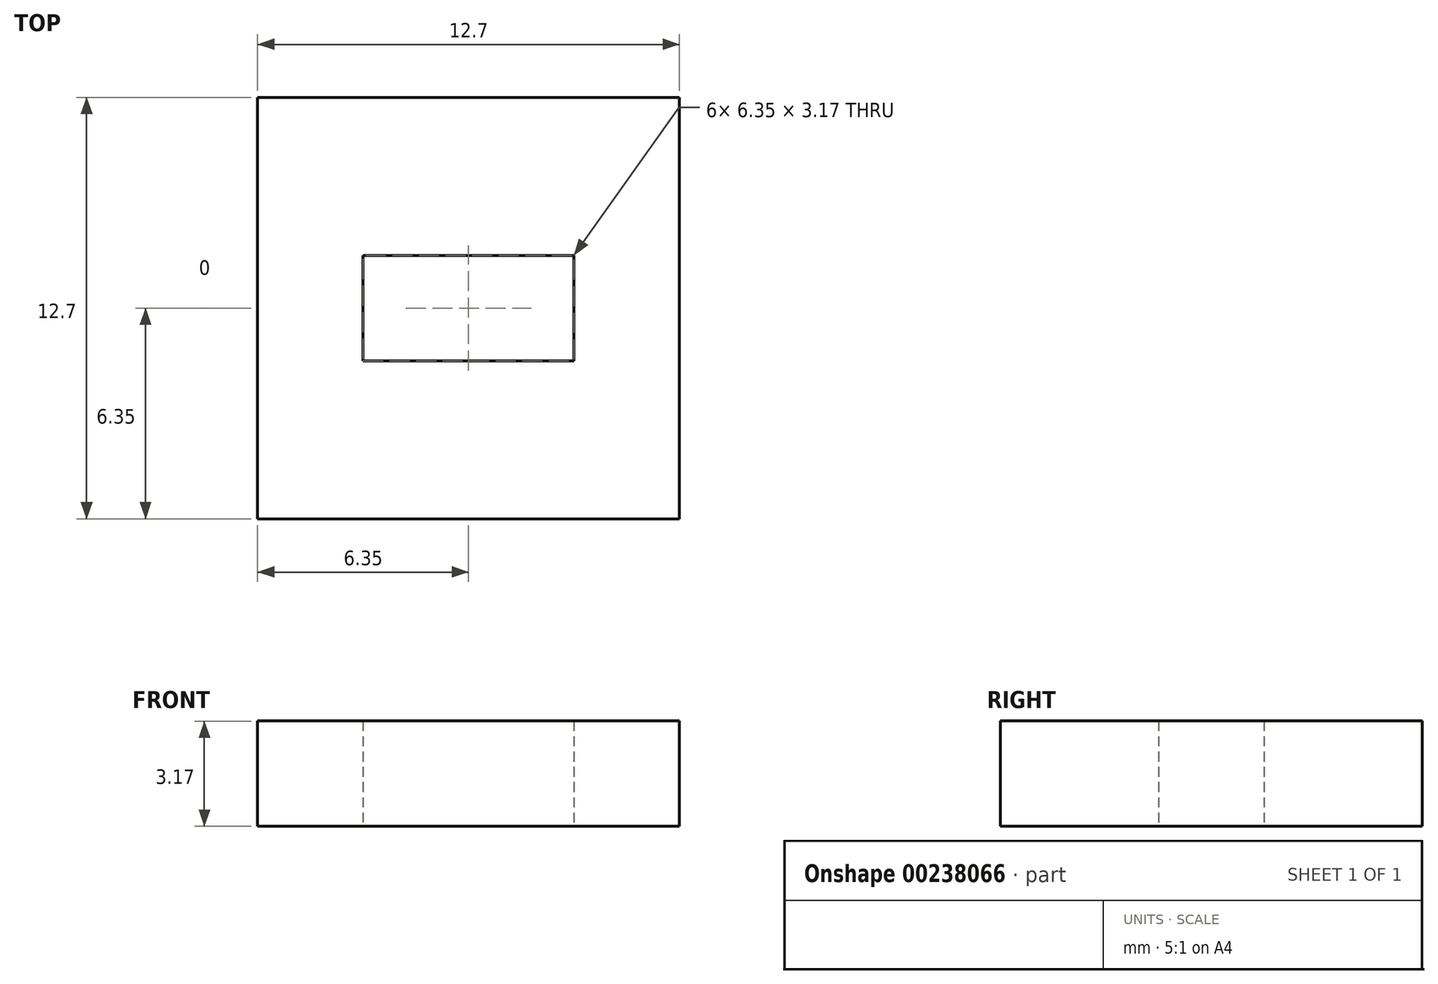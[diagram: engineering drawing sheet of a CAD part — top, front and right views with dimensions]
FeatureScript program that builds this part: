
annotation { "Feature Type Name" : "Feature", "Feature Type Description" : "" }
export const myFeature = defineFeature(function(context is Context, id is Id, definition is map)
    precondition{}
    {
        {
            var Q0;
            Q0=qCreatedBy(makeId("Top.planeOp"),FACE);
            var sketch = newSketch(context, id + "F0", { "sketchPlane" : qUnion([Q0])});
            skLineSegment(sketch, "E0.bottom", {"start": v(6.35, -6.35) * mm, "end": v(-6.35, -6.35) * mm});
            skLineSegment(sketch, "E0.top", {"start": v(6.35, 6.35) * mm, "end": v(-6.35, 6.35) * mm});
            skLineSegment(sketch, "E0.left", {"start": v(6.35, -6.35) * mm, "end": v(6.35, 6.35) * mm});
            skLineSegment(sketch, "E0.right", {"start": v(-6.35, -6.35) * mm, "end": v(-6.35, 6.35) * mm});
            skPoint(sketch, "E0.middle", {"position": v(0, 0) * mm});
            skLineSegment(sketch, "E1.bottom", {"start": v(3.18, -1.59) * mm, "end": v(-3.18, -1.59) * mm});
            skLineSegment(sketch, "E1.top", {"start": v(3.18, 1.59) * mm, "end": v(-3.18, 1.59) * mm});
            skLineSegment(sketch, "E1.left", {"start": v(3.18, -1.59) * mm, "end": v(3.18, 1.59) * mm});
            skLineSegment(sketch, "E1.right", {"start": v(-3.18, -1.59) * mm, "end": v(-3.18, 1.59) * mm});
            skSolve(sketch);
        }
        {
            var Q0;
            Q0=makeQuery(id+"F0.imprint","IMPRINT",FACE,{"disambiguationData":[TD([[makeQuery(id+"F0.imprint","IMPRINT",EDGE,{"derivedFrom":sQuery(id+"F0.wireOp",EDGE,"E0.bottom")}),-1.0]])]});
            extrude(context, id + "F1", {"entities" : qUnion([Q0]), "depth" : 3.17 * mm});
        }
    });
